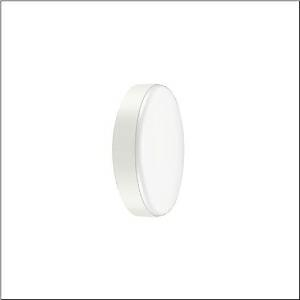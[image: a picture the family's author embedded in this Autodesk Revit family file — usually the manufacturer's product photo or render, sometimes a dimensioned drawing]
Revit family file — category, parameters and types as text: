
# Revit family: round_31_51wc10ma42as
name_source: partatom
category: Lighting Fixtures
units: mm (PartAtom-declared; Revit-internal decimal feet)

## family parameters
Cut with Voids When Loaded = No
Host = Face
Light Source = No
Part Type = Normal
Room Calculation Point = No
Round Connector Dimension = Use Diameter
Shared = No

## types (1)
- --- (1 x LED, 2550 lm, 20.5 W, 4000K)
    Apparent Load = 21 VA
    CIE Flux Codes = 44 75 94 94 100
    Color Rendering = 80
    Color Temperature = 4000K
    Default Elevation = 1800 mm
    Description = Round 31, wall and ceiling luminaire, primary optical cover: cover, of PC, opal, light emission: direct distribution, primary light characteristic: symmetric, installation type: surface-mounted, LED, rated luminous flux: 2.550lm, luminous efficacy: 124lm/W, light colour: 840, colour temperature: 4000K, control gear: ON/OFF Multilumen, with terminal, 3-pole, max. 2.5mm², mains connection: 220..240V, AC, 50/60Hz, rated input power: 20.5W, luminaire housing, of PC, traffic white (RAL 9016), diameter: 350mm, brightness and presence sensor, HF sensor, protection rating (complete): IP65, insulation class (complete): insulation class II (safety insulation), certification: CE, impact resistance: IK10, permissible operating ambient temperature: -20..+40°C, permissible storage temperature: -20..+60°C, packaging unit: 1 piece
    Height = 97 mm
    Lamp = 1 x LED
    Lamp Light Flux = 2550 lm
    Lamp Power = 20.5 W
    Lamp count = 1
    Length = 350 mm
    Luminous efficacy = 124 lm/W
    Manufacturer = Siteco
    ModVariant = No
    Model = 51WC10MA42AS
    Mounting Place = Ceiling
    Mounting Type = Surface mounted
    Number of Poles = 1
    OnlyDefault = Yes
    Power Factor = 1
    Product Name = Round 31
    Product group = wall and ceiling luminaire
    ProductGroupID = 304
    Protection Class = Protection class II
    Protection Degree = IP 65
    RLX_Detail_Level = 1
    RLX_Emergency_Light_Flux = 0 lm
    RLX_Emergency_Type = 0
    RLX_Emergency_Type_DB = No
    RlxData = <blob elided: 30481 chars, md5=994559f5>
    Socket = socket
    Standby Power = 0 W
    System Light Flux = 2550 lm
    System Power = 21 W
    Type Comments = factory setting: luminous flux: 100 % | (ON | ON)
    Type Image = l_1007027.jpg
    URL = http://relux.com
    VarID = @adj_150856
    Voltage = 0 V
    Weight = 0.00 kg
    Width = 0 mm  [stored 0 ft]

note: [stored X ft] marks values corroborated as IEEE doubles in the binary element streams (Revit-internal decimal feet)

## geometry (parser evidence)
native form markers: Blend x4, Sweep x12
no freeform markers — native parametric forms only
